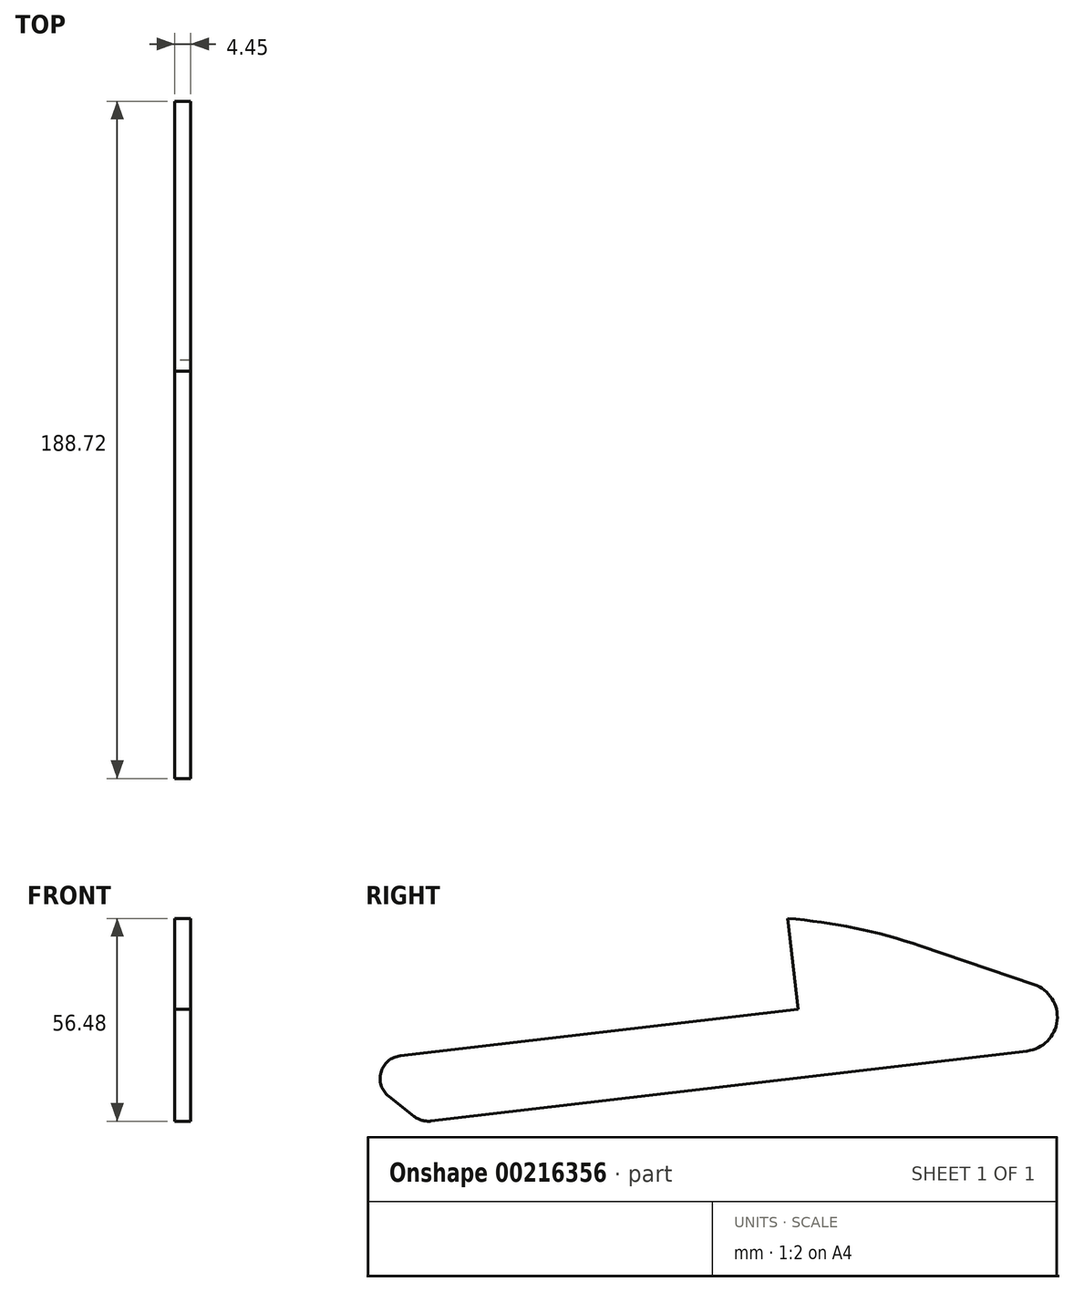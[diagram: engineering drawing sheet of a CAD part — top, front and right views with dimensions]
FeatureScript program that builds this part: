
annotation { "Feature Type Name" : "Feature", "Feature Type Description" : "" }
export const myFeature = defineFeature(function(context is Context, id is Id, definition is map)
    precondition{}
    {
        {
            var Q0;
            Q0=qCreatedBy(makeId("Right.planeOp"),FACE);
            var sketch = newSketch(context, id + "F0", { "sketchPlane" : qUnion([Q0])});
            skArc(sketch, "E0.0", {"start": v(-103.62, 21.66) * mm, "mid": v(-121.9, 26.64) * mm, "end": v(-140.64, 29.31) * mm});
            skLineSegment(sketch, "E1.0", {"start": v(-140.64, 29.31) * mm, "end": v(-137.67, 4.09) * mm});
            skLineSegment(sketch, "E2.0", {"start": v(-137.67, 4.09) * mm, "end": v(-248.58, -8.95) * mm});
            skLineSegment(sketch, "E3.0", {"start": v(-251.77, -20.24) * mm, "end": v(-244.72, -25.8) * mm});
            skArc(sketch, "E4.0", {"start": v(-244.72, -25.8) * mm, "mid": v(-242.52, -26.93) * mm, "end": v(-240.05, -27.13) * mm});
            skLineSegment(sketch, "E5.0", {"start": v(-240.05, -27.13) * mm, "end": v(-145.02, -15.96) * mm});
            skArc(sketch, "E6.0", {"start": v(-248.58, -8.95) * mm, "mid": v(-253.95, -13.53) * mm, "end": v(-251.77, -20.24) * mm});
            skLineSegment(sketch, "E7", {"start": v(-103.62, 21.66) * mm, "end": v(-71.93, 10.88) * mm});
            skLineSegment(sketch, "E8", {"start": v(-145.02, -15.96) * mm, "end": v(-73.89, -7.6) * mm});
            skPoint(sketch, "E9.visualSharp", {"position": v(-32.08, -2.68) * mm});
            skArc(sketch, "E9.filletArc", {"start": v(-73.89, -7.6) * mm, "mid": v(-65.53, 0.86) * mm, "end": v(-71.93, 10.88) * mm});
            skSolve(sketch);
        }
        {
            var Q0;
            Q0=makeQuery(id+"F0.imprint","IMPRINT",FACE,{"disambiguationData":[TD([[makeQuery(id+"F0.imprint","IMPRINT",EDGE,{"derivedFrom":sQuery(id+"F0.wireOp",EDGE,"E0.0")}),1.0]])]});
            extrude(context, id + "F1", {"entities" : qUnion([Q0]), "depth" : 4.44 * mm});
        }
    });
